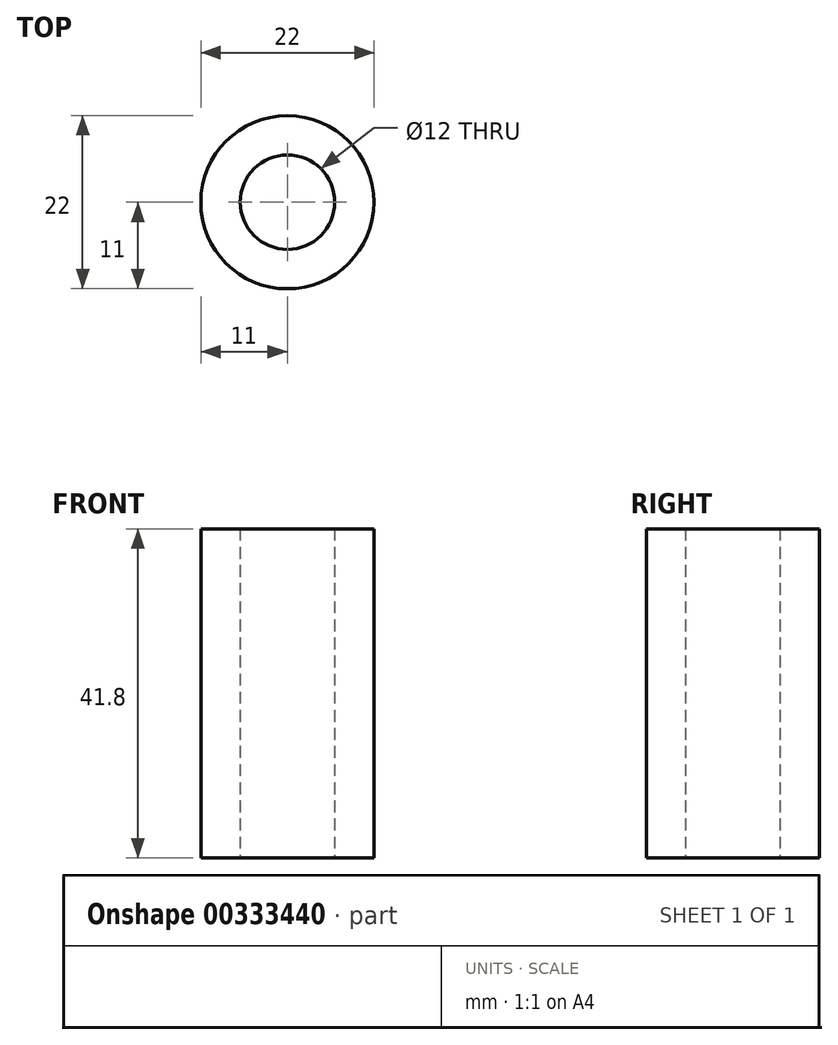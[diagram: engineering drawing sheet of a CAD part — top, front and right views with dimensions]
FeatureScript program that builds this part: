
annotation { "Feature Type Name" : "Feature", "Feature Type Description" : "" }
export const myFeature = defineFeature(function(context is Context, id is Id, definition is map)
    precondition{}
    {
        {
            var Q0;
            Q0=qCreatedBy(makeId("Top.planeOp"),FACE);
            var sketch = newSketch(context, id + "F0", { "sketchPlane" : qUnion([Q0])});
            skCircle(sketch, "E0", {"center": v(0, 0) * mm, "radius": 11 * mm});
            skCircle(sketch, "E1", {"center": v(0, 0) * mm, "radius": 6 * mm});
            skSolve(sketch);
        }
        {
            var Q0;
            Q0=makeQuery(id+"F0.imprint","IMPRINT",FACE,{"disambiguationData":[TD([[makeQuery(id+"F0.imprint","IMPRINT",EDGE,{"derivedFrom":sQuery(id+"F0.wireOp",EDGE,"E0")}),1.0]])]});
            extrude(context, id + "F1", {"entities" : qUnion([Q0]), "depth" : 41.8 * mm});
        }
    });
